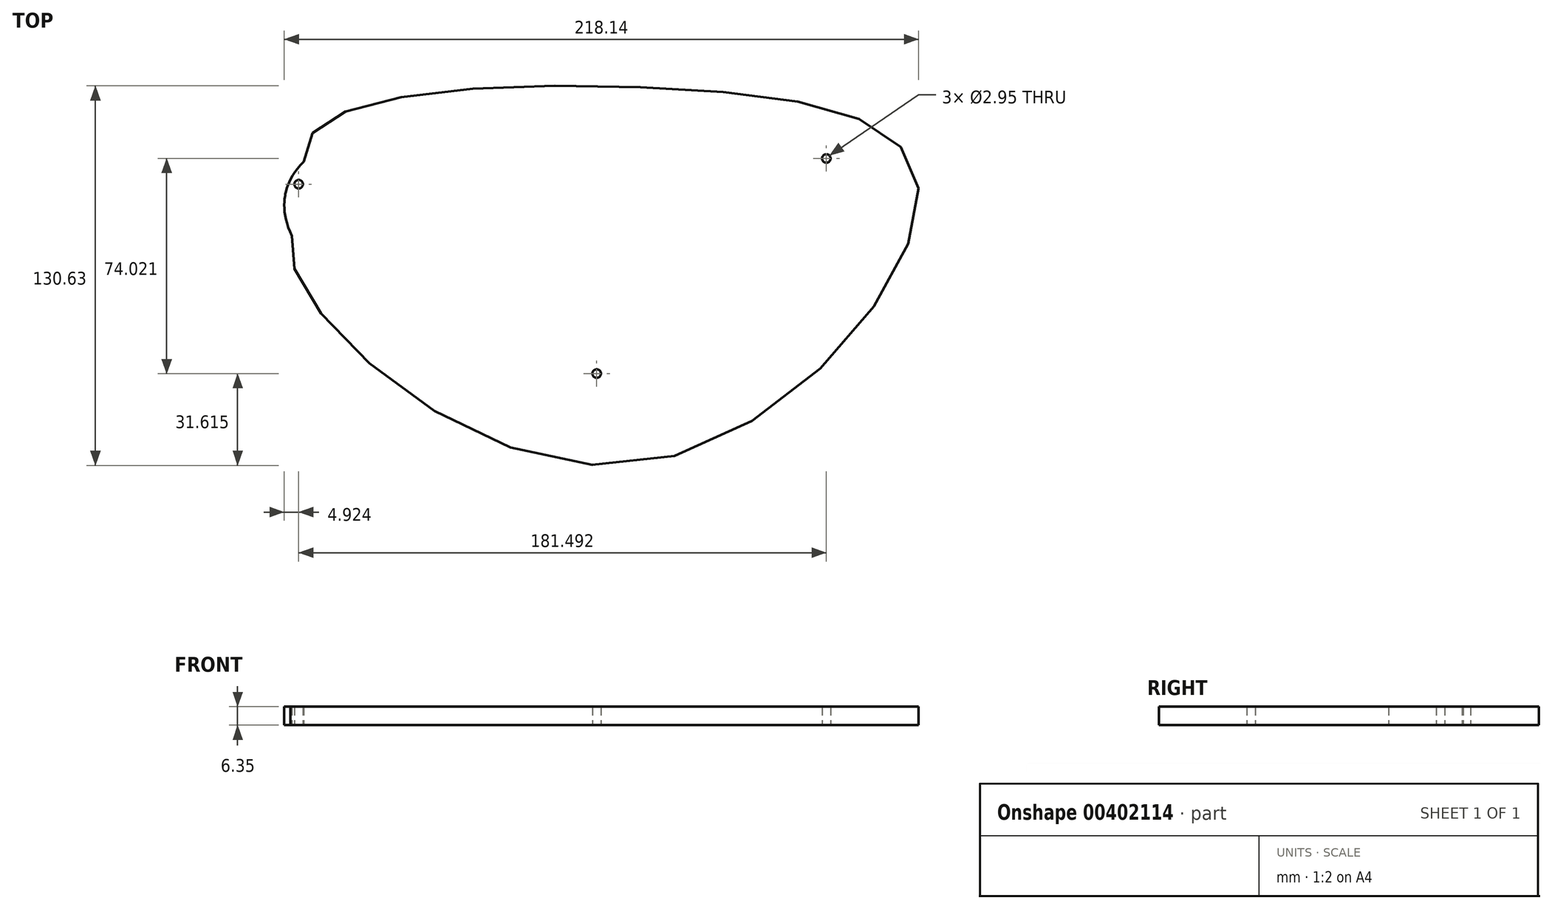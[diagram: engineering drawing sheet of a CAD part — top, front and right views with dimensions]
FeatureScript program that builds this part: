
annotation { "Feature Type Name" : "Feature", "Feature Type Description" : "" }
export const myFeature = defineFeature(function(context is Context, id is Id, definition is map)
    precondition{}
    {
        {
            var Q0;
            Q0=qCreatedBy(makeId("Top.planeOp"),FACE);
            var sketch = newSketch(context, id + "F0", { "sketchPlane" : qUnion([Q0])});
            skPoint(sketch, "E0", {"position": v(-95.25, 18.2) * mm});
            skLineSegment(sketch, "E1", {"start": v(-95.25, 18.2) * mm, "end": v(-92.41, 16.77) * mm, "construction": true});
            skLineSegment(sketch, "E2", {"start": v(-92.41, 16.77) * mm, "end": v(-88.33, 24.82) * mm, "construction": true});
            skPoint(sketch, "E3", {"position": v(7.26, -46.94) * mm});
            skLineSegment(sketch, "E4", {"start": v(7.26, -46.94) * mm, "end": v(7.3, -43.77) * mm, "construction": true});
            skLineSegment(sketch, "E5", {"start": v(7.3, -43.77) * mm, "end": v(5.33, -43.75) * mm, "construction": true});
            skPoint(sketch, "E6", {"position": v(86.25, 27.08) * mm});
            skLineSegment(sketch, "E7", {"start": v(86.25, 27.08) * mm, "end": v(84, 24.83) * mm, "construction": true});
            skLineSegment(sketch, "E8", {"start": v(84, 24.83) * mm, "end": v(93.02, 15.82) * mm, "construction": true});
            skFitSpline(sketch, "E9.0", {"points": [v(-99.92, 13.97) * mm, v(-100, 13.48) * mm, v(-100.1, 12.49) * mm, v(-100.17, 10.5) * mm, v(-99.97, 8.05) * mm, v(-99.33, 5.18) * mm, v(-98.03, 1.46) * mm, v(-95.66, -3) * mm, v(-91.85, -8.12) * mm, v(-87.17, -13.08) * mm, v(-81.72, -17.9) * mm, v(-75.55, -22.56) * mm, v(-66.48, -28.52) * mm, v(-53.74, -35.38) * mm, v(-39.64, -41.13) * mm, v(-27.85, -44.83) * mm, v(-18.84, -47.1) * mm, v(-9.73, -48.8) * mm, v(-0.59, -49.88) * mm, v(6.98, -50.2) * mm, v(12.98, -50.05) * mm, v(18.9, -49.65) * mm, v(26.13, -48.65) * mm, v(34.48, -46.76) * mm, v(42.45, -44.24) * mm, v(52.55, -40.15) * mm, v(64.07, -33.82) * mm, v(75.85, -24.83) * mm, v(83.74, -16.59) * mm, v(88.76, -9.74) * mm, v(91.84, -4.52) * mm, v(94.18, 0.76) * mm, v(95.44, 5.2) * mm, v(96, 8.76) * mm, v(96.15, 11.44) * mm, v(96.03, 14.1) * mm, v(95.49, 17.57) * mm, v(94.1, 21.7) * mm, v(91.44, 26.16) * mm, v(87.95, 30.04) * mm, v(83.79, 33.39) * mm, v(79.03, 36.27) * mm, v(71.94, 39.6) * mm, v(61.77, 42.9) * mm, v(47.59, 45.71) * mm, v(31.6, 47.5) * mm, v(14.04, 48.34) * mm, v(-4.44, 48.21) * mm, v(-23.1, 47.11) * mm, v(-41.24, 45) * mm, v(-55.34, 42.4) * mm, v(-65.69, 39.75) * mm, v(-72.9, 37.48) * mm, v(-79.5, 34.89) * mm, v(-85.42, 31.93) * mm, v(-90.6, 28.53) * mm, v(-94.25, 25.2) * mm, v(-96.66, 22.14) * mm, v(-98.16, 19.63) * mm, v(-99.1, 17.36) * mm, v(-99.65, 15.45) * mm, v(-99.84, 14.47) * mm, v(-99.92, 13.97) * mm]});
            skFitSpline(sketch, "E10.0", {"points": [v(-93.64, 13) * mm, v(-97.14, -9.6) * mm, v(18.18, -78.26) * mm, v(117.8, 17.88) * mm, v(33.69, 51.07) * mm, v(-90.05, 36.27) * mm, v(-93.64, 13) * mm]});
            skSolve(sketch);
        }
        {
            var Q0;
            Q0=makeQuery(id+"F0.imprint","IMPRINT",FACE,{"disambiguationData":[TD([[makeQuery(id+"F0.imprint","IMPRINT",EDGE,{"derivedFrom":sQuery(id+"F0.wireOp",EDGE,"E10.0")}),1.0]])]});
            var Q1;
            Q1=makeQuery(id+"F0.imprint","IMPRINT",FACE,{"disambiguationData":[TD([[makeQuery(id+"F0.imprint","IMPRINT",EDGE,{"derivedFrom":sQuery(id+"F0.wireOp",EDGE,"E9.0")}),1.0]])]});
            extrude(context, id + "F1", {"entities" : qUnion([Q0, Q1]), "depth" : 6.35 * mm});
        }
        {
            var Q0;
            Q0=sQuery(id+"F0.wireOp",VERTEX,"E0");
            var Q1;
            Q1=sQuery(id+"F0.wireOp",VERTEX,"E6");
            var Q2;
            Q2=sQuery(id+"F0.wireOp",VERTEX,"E3");
            var Q3;
            Q3=makeQuery(id+"F1.opExtrude","SWEPT_BODY",BODY,{"disambiguationData":[OSD([sQuery(id+"F0.wireOp",EDGE,"E9.0")])]});
            hole(context, id + "F2", {"style" : HoleStyle.SIMPLE, "endStyle" : HoleEndStyle.BLIND, "oppositeDirection" : true, "standardTappedOrClearance" : lookupTablePath({ "standard" : "ANSI", "fit" : "Close", "size" : "#4", "type" : "Clearance" }), "standardBlindInLast" : lookupTablePath({ "fit" : "Close", "standard" : "ANSI", "size" : "#4", "type" : "Clearance" }), "holeDiameter" : 2.95 * mm, "holeDepth" : 6.35 * mm, "startFromSketch" : true, "locations" : qUnion([Q0, Q1, Q2]), "scope" : qUnion([Q3])});
        }
    });
